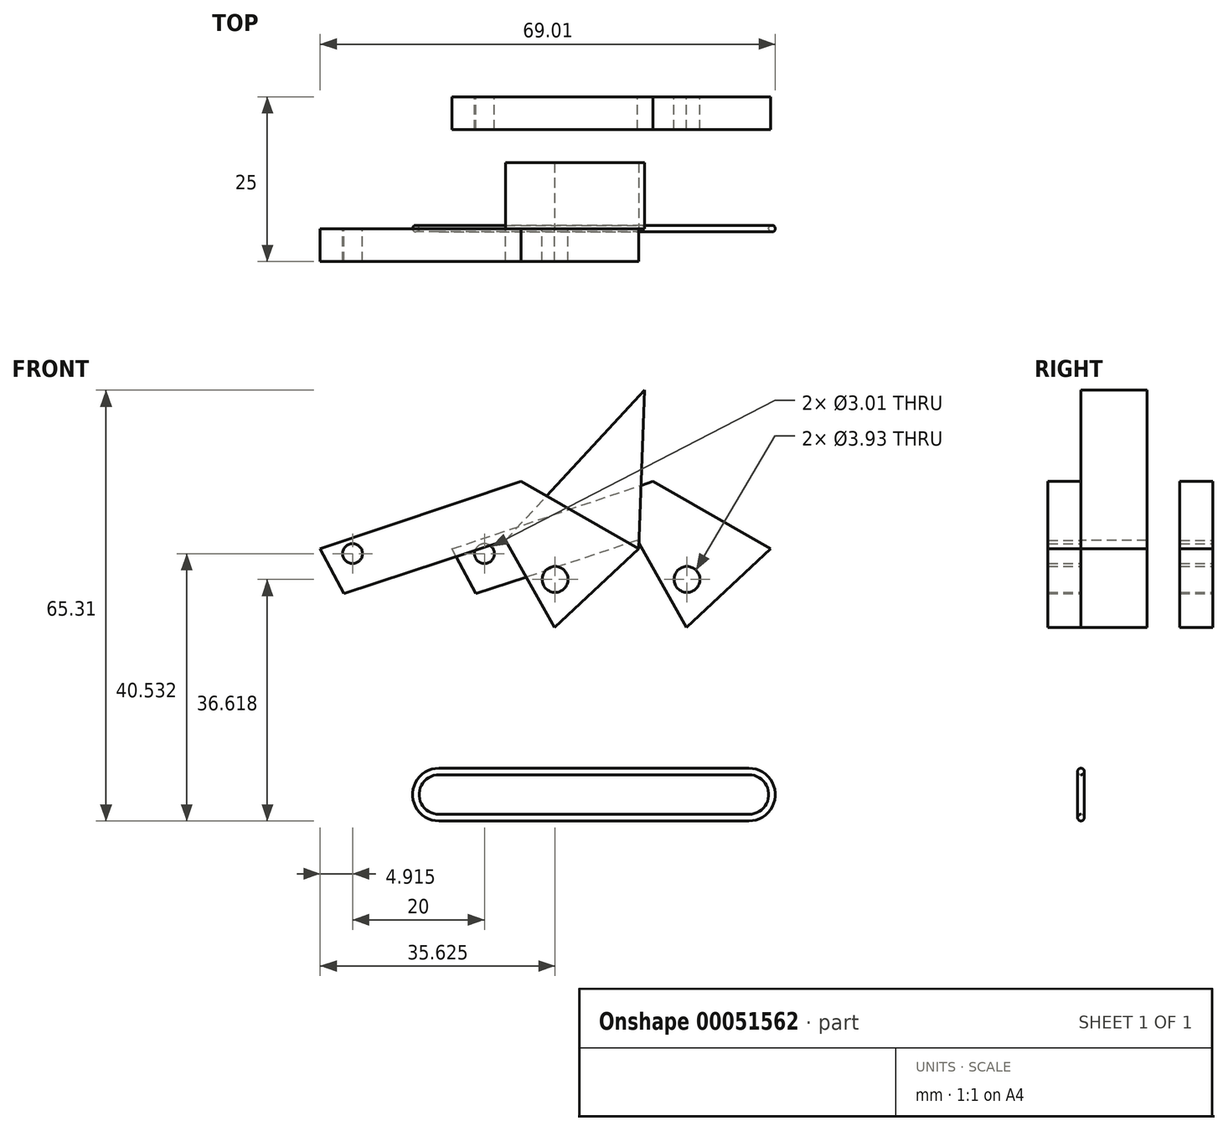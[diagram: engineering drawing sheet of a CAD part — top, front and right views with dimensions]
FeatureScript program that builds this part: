
annotation { "Feature Type Name" : "Feature", "Feature Type Description" : "" }
export const myFeature = defineFeature(function(context is Context, id is Id, definition is map)
    precondition{}
    {
        {
            var Q0;
            Q0=qCreatedBy(makeId("Front.planeOp"),FACE);
            var sketch = newSketch(context, id + "F0", { "sketchPlane" : qUnion([Q0])});
            skLineSegment(sketch, "E0", {"start": v(-23.5, 0) * mm, "end": v(23.5, 0) * mm});
            skArc(sketch, "E1.0.startCap", {"start": v(-23.5, -3.5) * mm, "mid": v(-27, 0) * mm, "end": v(-23.5, 3.5) * mm});
            skArc(sketch, "E1.0.endCap", {"start": v(23.5, 3.5) * mm, "mid": v(27, 0) * mm, "end": v(23.5, -3.5) * mm});
            skLineSegment(sketch, "E1.0.left", {"start": v(-23.5, 3.5) * mm, "end": v(23.5, 3.5) * mm});
            skLineSegment(sketch, "E1.0.right", {"start": v(-23.5, -3.5) * mm, "end": v(23.5, -3.5) * mm});
            skSolve(sketch);
        }
        {
            var Q0;
            Q0=sQuery(id+"F0.wireOp",VERTEX,"E1.0.startCap.center");
            var Q1;
            Q1=sQuery(id+"F0.wireOp",EDGE,"E0");
            cPlane(context, id + "F1", {"entities" : qUnion([Q0, Q1]), "cplaneType" : CPlaneType.LINE_POINT, "offset" : 150 * mm, "width" : 150 * mm, "height" : 150 * mm});
        }
        {
            var Q0;
            Q0=qCreatedBy(id+"F1.planeOp",FACE);
            var sketch = newSketch(context, id + "F2", { "sketchPlane" : qUnion([Q0])});
            skCircle(sketch, "E2", {"center": v(0, 3.5) * mm, "radius": 0.5 * mm});
            skSolve(sketch);
        }
        {
            var Q0;
            Q0=makeQuery(id+"F2.imprint","IMPRINT",FACE,{"disambiguationData":[TD([[makeQuery(id+"F2.imprint","IMPRINT",EDGE,{"derivedFrom":sQuery(id+"F2.wireOp",EDGE,"E2")}),1.0]])]});
            var Q1;
            Q1=sQuery(id+"F0.wireOp",EDGE,"E1.0.left");
            var Q2;
            Q2=sQuery(id+"F0.wireOp",EDGE,"E1.0.endCap");
            var Q3;
            Q3=sQuery(id+"F0.wireOp",EDGE,"E1.0.right");
            var Q4;
            Q4=sQuery(id+"F0.wireOp",EDGE,"E1.0.startCap");
            sweep(context, id + "F3", {"profiles" : qUnion([Q0]), "path" : qUnion([Q1, Q2, Q3, Q4])});
        }
        {
            var Q0;
            Q0=qCreatedBy(makeId("Front.planeOp"),FACE);
            var sketch = newSketch(context, id + "F4", { "sketchPlane" : qUnion([Q0])});
            skLineSegment(sketch, "E3", {"start": v(-41.51, 37.26) * mm, "end": v(-11.07, 47.47) * mm});
            skLineSegment(sketch, "E4", {"start": v(-11.07, 47.47) * mm, "end": v(6.81, 37.26) * mm});
            skLineSegment(sketch, "E5", {"start": v(6.81, 37.26) * mm, "end": v(-5.96, 25.33) * mm});
            skLineSegment(sketch, "E6", {"start": v(-5.96, 25.33) * mm, "end": v(-13.41, 38.53) * mm});
            skLineSegment(sketch, "E7", {"start": v(-13.41, 38.53) * mm, "end": v(-37.9, 30.44) * mm});
            skLineSegment(sketch, "E8", {"start": v(-37.9, 30.44) * mm, "end": v(-41.51, 37.26) * mm});
            skLineSegment(sketch, "E9", {"start": v(-13.41, 38.53) * mm, "end": v(7.66, 61.31) * mm});
            skLineSegment(sketch, "E10", {"start": v(7.66, 61.31) * mm, "end": v(6.81, 37.26) * mm});
            skCircle(sketch, "E11", {"center": v(-36.6, 36.53) * mm, "radius": 1.5 * mm});
            skCircle(sketch, "E12", {"center": v(-5.89, 32.62) * mm, "radius": 1.96 * mm});
            skSolve(sketch);
        }
        {
            var Q0;
            {var subQ2=sQuery(id+"F4.wireOp",EDGE,"E3");Q0=makeQuery(id+"F4.imprint","IMPRINT",FACE,{"disambiguationData":[TD([[makeQuery(id+"F4.imprint","IMPRINT",EDGE,{"derivedFrom":subQ2}),-1.0]])]});}
            var Q1;
            {var subQ4=sQuery(id+"F4.wireOp",EDGE,"E5");Q1=makeQuery(id+"F4.imprint","IMPRINT",FACE,{"disambiguationData":[TD([[makeQuery(id+"F4.imprint","IMPRINT",EDGE,{"derivedFrom":subQ4}),-1.0]])]});}
            extrude(context, id + "F5", {"entities" : qUnion([Q0, Q1]), "depth" : 5 * mm});
        }
        {
            var Q0;
            Q0 = qSketchRegion(id + "F4", true);
            extrude(context, id + "F6", {"entities" : qUnion([Q0]), "depth" : 25 * mm});
        }
        {
            var Q0;
            Q0=makeQuery(id+"F6.opExtrude","SWEPT_BODY",BODY,{"disambiguationData":[OSD([sQuery(id+"F4.wireOp",EDGE,"E3"),sQuery(id+"F4.wireOp",EDGE,"E4"),sQuery(id+"F4.wireOp",EDGE,"E5"),sQuery(id+"F4.wireOp",EDGE,"E6"),sQuery(id+"F4.wireOp",EDGE,"E7"),sQuery(id+"F4.wireOp",EDGE,"E8"),sQuery(id+"F4.wireOp",EDGE,"E9"),sQuery(id+"F4.wireOp",EDGE,"E10"),sQuery(id+"F4.wireOp",EDGE,"E11"),sQuery(id+"F4.wireOp",EDGE,"E12")])]});
            deleteBodies(context, id + "F7", {"entities" : qUnion([Q0])});
        }
        {
            var Q0;
            {var subQ0=sQuery(id+"F4.wireOp",EDGE,"E10");Q0=makeQuery(id+"F4.imprint","IMPRINT",FACE,{"disambiguationData":[TD([[makeQuery(id+"F4.imprint","IMPRINT",EDGE,{"derivedFrom":subQ0}),-1.0]])]});}
            var Q1;
            {var subQ4=sQuery(id+"F4.wireOp",EDGE,"E5");Q1=makeQuery(id+"F4.imprint","IMPRINT",FACE,{"disambiguationData":[TD([[makeQuery(id+"F4.imprint","IMPRINT",EDGE,{"derivedFrom":subQ4}),-1.0]])]});}
            extrude(context, id + "F8", {"entities" : qUnion([Q0, Q1]), "depth" : 10 * mm});
        }
        {
            var Q0;
            Q0=makeQuery(id+"F8.opExtrude","SWEPT_BODY",BODY,{"disambiguationData":[OSD([sQuery(id+"F4.wireOp",EDGE,"E5"),sQuery(id+"F4.wireOp",EDGE,"E6"),sQuery(id+"F4.wireOp",EDGE,"E9"),sQuery(id+"F4.wireOp",EDGE,"E10"),sQuery(id+"F4.wireOp",EDGE,"E12")])]});
            deleteBodies(context, id + "F9", {"entities" : qUnion([Q0])});
        }
        {
            var Q0;
            {var subQ0=sQuery(id+"F4.wireOp",EDGE,"E10");Q0=makeQuery(id+"F4.imprint","IMPRINT",FACE,{"disambiguationData":[TD([[makeQuery(id+"F4.imprint","IMPRINT",EDGE,{"derivedFrom":subQ0}),-1.0]])]});}
            var Q1;
            {var subQ4=sQuery(id+"F4.wireOp",EDGE,"E5");Q1=makeQuery(id+"F4.imprint","IMPRINT",FACE,{"disambiguationData":[TD([[makeQuery(id+"F4.imprint","IMPRINT",EDGE,{"derivedFrom":subQ4}),-1.0]])]});}
            var Q2;
            Q2=makeQuery(id+"F4.imprint","IMPRINT",FACE,{"disambiguationData":[TD([[makeQuery(id+"F4.imprint","IMPRINT",EDGE,{"derivedFrom":sQuery(id+"F4.wireOp",EDGE,"E12")}),1.0]])]});
            extrude(context, id + "F10", {"entities" : qUnion([Q0, Q1, Q2]), "oppositeDirection" : true, "depth" : 10 * mm});
        }
        {
            var Q0;
            Q0=makeQuery(id+"F5.opExtrude","SWEPT_BODY",BODY,{"disambiguationData":[OSD([sQuery(id+"F4.wireOp",EDGE,"E3"),sQuery(id+"F4.wireOp",EDGE,"E4"),sQuery(id+"F4.wireOp",EDGE,"E5"),sQuery(id+"F4.wireOp",EDGE,"E6"),sQuery(id+"F4.wireOp",EDGE,"E7"),sQuery(id+"F4.wireOp",EDGE,"E8"),sQuery(id+"F4.wireOp",EDGE,"E11"),sQuery(id+"F4.wireOp",EDGE,"E12")])]});
            transform(context, id + "F11", {"entities" : qUnion([Q0]), "transformType" : TransformType.TRANSLATION_3D, "dx" : 20 * mm, "dy" : 20 * mm, "dz" : 0 * mm, "makeCopy" : true});
        }
    });
